# Revit family: CONTURA II 1700 FS BTW Bath
name_source: partatom
category: Plumbing Fixtures
units: mm (PartAtom-declared; Revit-internal decimal feet)

## family parameters
Cut with Voids When Loaded = Yes
Host = Face
OmniClass Number = 23.45.05.14.21
OmniClass Title = Bathtubs
Part Type = Normal
Room Calculation Point = No
Round Connector Dimension = Use Diameter
Shared = No

## types (3) — shared parameters
Assembly Code = D2010510
CW Connection = No
HW Connection = No
Manufacturer = GWA Bathrooms & Kitchens
Material_Waste = GWA-Metalwork-White
URL = https://www.caroma.com.au
Vent Connection = No
Waste Connection = Yes
zero-valued in all types: Default Elevation

## per-type parameters (varying)
| type | Material_Bath | Model |
| CONTURA II 1700 FS BTW Bath - MATTE CLAY | GWA-Acrylic-Matte-Clay | CII7WFMC |
| CONTURA II 1700 FS BTW Bath - MATTE WHITE | GWA-Acrylic-Matte-White | CII7WFMW |
| CONTURA II 1700 FS BTW Bath - WHITE | GWA-Acrylic-White | CII7WFW |

note: column(s) folded — value = type name in every type: Description

## geometry (parser evidence)
native form markers: Sweep x2
no freeform markers — native parametric forms only
